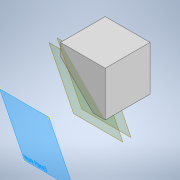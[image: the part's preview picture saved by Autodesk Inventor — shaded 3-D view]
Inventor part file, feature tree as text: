
AUTODESK INVENTOR PART (.ipt)
format: ipt  version: 2022 (Build 260153000, 153)  size: 247,296 bytes
history: native  units: mm
features: extrude x5, sketch x5, plane x2, fillet x2
ambient origin geometry x8: Origin, YZ Plane, XZ Plane, XY Plane, X Axis, Y Axis, Z Axis, Center Point
bodies: Body1 (feature_tree)
feature tree (14):
  extrude  "Extrusion8"  Depth=22.0mm
  plane  "Work Plane4"
  extrude  "Extrusion11"  Depth=11.0mm
  extrude  "Extrusion12"  Depth=5.0mm
  extrude  "Extrusion13"  Depth=5.0mm
  extrude  "Extrusion14"  Depth=5.0mm
  fillet  "Fillet1"  Radius=29.75mm
  fillet  "Fillet2"  Radius=22.0mm
  sketch  "Sketch11"  dims[d39=22.0mm d40=22.0mm]
  plane  "Work Plane3"
  sketch  "Sketch14"  dims[d41=11.0mm d42=11.0mm]
  sketch  "Sketch16"  dims[d43=5.0mm d44=5.0mm]
  sketch  "Sketch17"  dims[d45=5.0mm d46=5.0mm]
  sketch  "Sketch18"  dims[d47=32.0mm d48=0.0mm d57=5.0mm d58=29.75mm d59=0.0mm d60=22.0mm d61=22.0mm d62=11.0mm d63=11.0mm d64=50.0mm d65=0.0mm d66=22.0mm d67=22.0mm d68=5.0mm d69=5.0mm d70=50.0mm d71=0.0mm d72=22.0mm d73=22.0mm d74=5.0mm d75=5.0mm d76=50.0mm d77=0.0mm d78=5.0mm d79=5.0mm d33=0.5mm d34=0.872665mm d35=0.5mm d36=0.872665mm]
